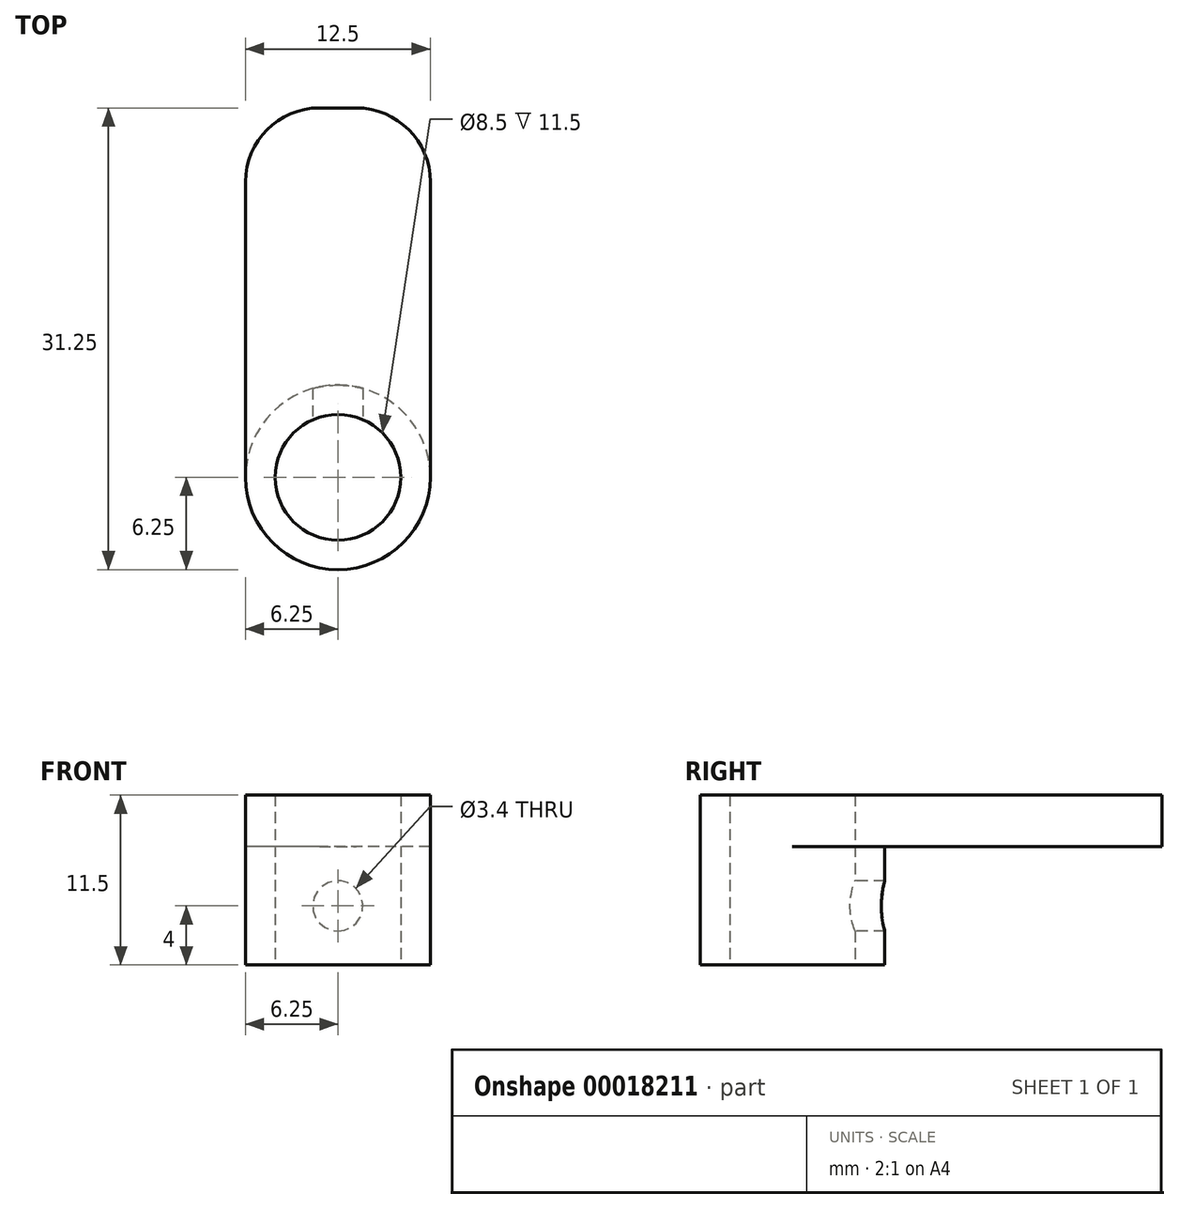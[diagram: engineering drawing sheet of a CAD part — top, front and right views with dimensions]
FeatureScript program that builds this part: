
annotation { "Feature Type Name" : "Feature", "Feature Type Description" : "" }
export const myFeature = defineFeature(function(context is Context, id is Id, definition is map)
    precondition{}
    {
        {
            var Q0;
            Q0=qCreatedBy(makeId("Top.planeOp"),FACE);
            var sketch = newSketch(context, id + "F0", { "sketchPlane" : qUnion([Q0])});
            skCircle(sketch, "E0", {"center": v(0, 0) * mm, "radius": 4.25 * mm});
            skCircle(sketch, "E1", {"center": v(0, 0) * mm, "radius": 6.25 * mm});
            skSolve(sketch);
        }
        {
            var Q0;
            Q0 = qSketchRegion(id + "F0", true);
            extrude(context, id + "F1", {"entities" : qUnion([Q0]), "depth" : 8 * mm});
        }
        {
            var Q0;
            Q0=makeQuery(id+"F1.opExtrude","CAP_FACE",FACE,{"disambiguationData":[OSD([sQuery(id+"F0.wireOp",EDGE,"E0"),sQuery(id+"F0.wireOp",EDGE,"E1")])],"isStart":false});
            var sketch = newSketch(context, id + "F2", { "sketchPlane" : qUnion([Q0])});
            skLineSegment(sketch, "E2.bottom", {"start": v(-6.25, 0) * mm, "end": v(6.25, 0) * mm});
            skLineSegment(sketch, "E2.top", {"start": v(-1.25, 25) * mm, "end": v(1.25, 25) * mm});
            skLineSegment(sketch, "E2.left", {"start": v(-6.25, 0) * mm, "end": v(-6.25, 20) * mm});
            skLineSegment(sketch, "E2.right", {"start": v(6.25, 0) * mm, "end": v(6.25, 20) * mm});
            skPoint(sketch, "E3.visualSharp", {"position": v(6.25, 25) * mm});
            skArc(sketch, "E3.filletArc", {"start": v(6.25, 20) * mm, "mid": v(4.79, 23.54) * mm, "end": v(1.25, 25) * mm});
            skPoint(sketch, "E4.visualSharp", {"position": v(-6.25, 25) * mm});
            skArc(sketch, "E4.filletArc", {"start": v(-1.25, 25) * mm, "mid": v(-4.79, 23.54) * mm, "end": v(-6.25, 20) * mm});
            skSolve(sketch);
        }
        {
            var Q0;
            Q0=makeQuery(id+"F2.imprint","IMPRINT",FACE,{"disambiguationData":[TD([[makeQuery(id+"F2.imprint","IMPRINT",EDGE,{"derivedFrom":sQuery(id+"F2.wireOp",EDGE,"E2.top")}),-1.0]])]});
            var Q1;
            {var subQ0=makeQuery(id+"F1.opExtrude","CAP_EDGE",EDGE,{"disambiguationData":[OSD([sQuery(id+"F0.wireOp",EDGE,"E0")])],"isStart":false});var subQ1=sQuery(id+"F2.wireOp",EDGE,"E2.bottom");var subQ3=makeQuery(id+"F2.imprint","INTERSECT",VERTEX,{"disambiguationData":[OD(0.0)],"derivedFrom":[subQ0,subQ1]});Q1=makeQuery(id+"F2.imprint","IMPRINT",FACE,{"disambiguationData":[TD([[makeQuery(id+"F2.imprint","IMPRINT",EDGE,{"disambiguationData":[TD([[subQ3,1.0]])],"derivedFrom":subQ0}),-1.0]])]});}
            var Q2;
            {var subQ0=makeQuery(id+"F1.opExtrude","CAP_EDGE",EDGE,{"disambiguationData":[OSD([sQuery(id+"F0.wireOp",EDGE,"E0")])],"isStart":false});var subQ1=sQuery(id+"F2.wireOp",EDGE,"E2.bottom");var subQ3=makeQuery(id+"F2.imprint","INTERSECT",VERTEX,{"disambiguationData":[OD(0.0)],"derivedFrom":[subQ0,subQ1]});Q2=makeQuery(id+"F2.imprint","IMPRINT",FACE,{"disambiguationData":[TD([[makeQuery(id+"F2.imprint","IMPRINT",EDGE,{"disambiguationData":[TD([[subQ3,-1.0]])],"derivedFrom":subQ0}),-1.0]])]});}
            extrude(context, id + "F3", {"entities" : qUnion([Q0, Q1, Q2]), "operationType" : NewBodyOperationType.ADD, "depth" : 3.5 * mm});
        }
        {
            var Q0;
            Q0=qCreatedBy(makeId("Front.planeOp"),FACE);
            var sketch = newSketch(context, id + "F4", { "sketchPlane" : qUnion([Q0])});
            skCircle(sketch, "E5", {"center": v(0, 4) * mm, "radius": 1.7 * mm});
            skSolve(sketch);
        }
        {
            var Q0;
            Q0 = qSketchRegion(id + "F4", true);
            extrude(context, id + "F5", {"entities" : qUnion([Q0]), "operationType" : NewBodyOperationType.REMOVE, "oppositeDirection" : true, "depth" : 25 * mm});
        }
    });
